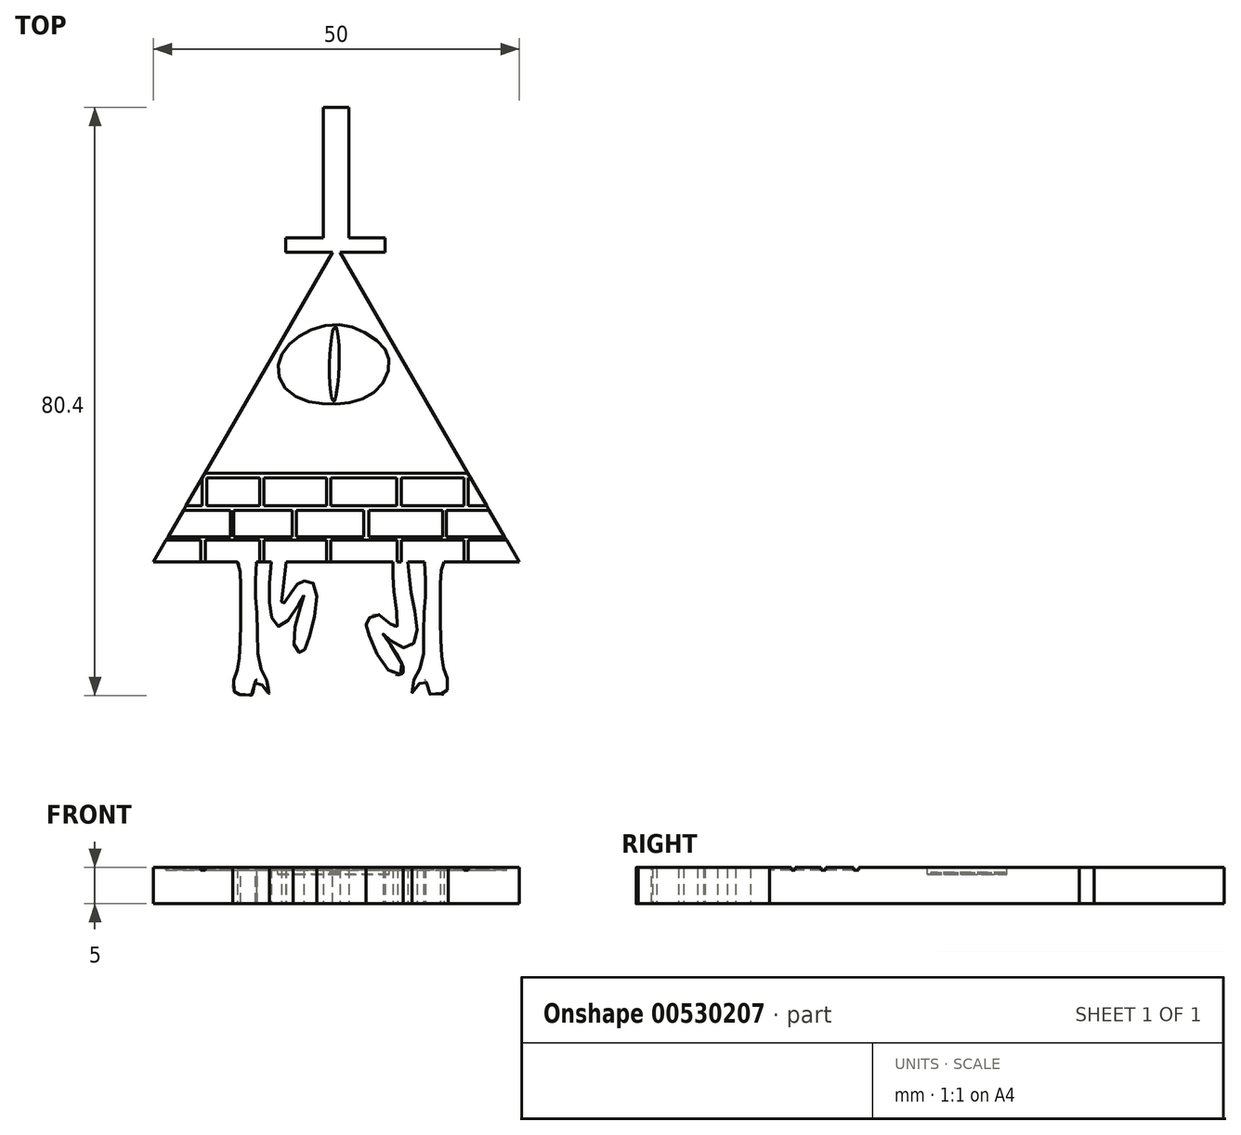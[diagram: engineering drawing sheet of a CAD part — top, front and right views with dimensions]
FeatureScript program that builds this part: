
annotation { "Feature Type Name" : "Feature", "Feature Type Description" : "" }
export const myFeature = defineFeature(function(context is Context, id is Id, definition is map)
    precondition{}
    {
        {
            var Q0;
            Q0=qCreatedBy(makeId("Top.planeOp"),FACE);
            var sketch = newSketch(context, id + "F0", { "sketchPlane" : qUnion([Q0])});
            skLineSegment(sketch, "E0", {"start": v(0, 43.3) * mm, "end": v(-25, 0) * mm});
            skLineSegment(sketch, "E1", {"start": v(-25, 0) * mm, "end": v(25, 0) * mm});
            skLineSegment(sketch, "E2", {"start": v(25, 0) * mm, "end": v(0, 43.3) * mm});
            skLineSegment(sketch, "E3.bottom", {"start": v(-6.91, 44.37) * mm, "end": v(6.68, 44.37) * mm});
            skLineSegment(sketch, "E3.top", {"start": v(-6.91, 42.4) * mm, "end": v(6.68, 42.4) * mm});
            skLineSegment(sketch, "E3.left", {"start": v(-6.91, 44.37) * mm, "end": v(-6.91, 42.4) * mm});
            skLineSegment(sketch, "E3.right", {"start": v(6.68, 44.37) * mm, "end": v(6.68, 42.4) * mm});
            skLineSegment(sketch, "E4.bottom", {"start": v(-1.76, 62.16) * mm, "end": v(1.7, 62.16) * mm});
            skLineSegment(sketch, "E4.top", {"start": v(-1.76, 42.4) * mm, "end": v(1.7, 42.4) * mm});
            skLineSegment(sketch, "E4.left", {"start": v(-1.76, 62.16) * mm, "end": v(-1.76, 42.4) * mm});
            skLineSegment(sketch, "E4.right", {"start": v(1.7, 62.16) * mm, "end": v(1.7, 42.4) * mm});
            skFitSpline(sketch, "E5", {"points": [v(-8.9, 0) * mm, v(-8.8, -7.65) * mm, v(-7.35, -8.7) * mm, v(-4.44, -4.65) * mm, v(-5.9, -10.56) * mm, v(-4.86, -12.43) * mm, v(-3.82, -10.66) * mm, v(-2.99, -3.09) * mm, v(-4.75, -2.67) * mm, v(-5.69, -3.5) * mm, v(-7.35, -5.79) * mm, v(-6.83, 0) * mm], "startDerivative": vector(-6.57, -68.42) * mm, "endDerivative": vector(6.6, 85.35) * mm});
            skFitSpline(sketch, "E6", {"points": [v(7.74, 0) * mm, v(7.95, -4.5) * mm, v(8.14, -8.99) * mm, v(5.66, -7.15) * mm, v(4.23, -8.08) * mm, v(4.23, -9.3) * mm, v(7.54, -15.12) * mm, v(9.17, -14.8) * mm, v(6.4, -9.85) * mm, v(8.68, -11.58) * mm, v(10.84, -10.66) * mm, v(10.34, -4.69) * mm, v(9.8, 0) * mm], "startDerivative": vector(0.32, -42.65) * mm, "endDerivative": vector(-4.02, 37.85) * mm});
            skFitSpline(sketch, "E7.MirrorCS", {"points": [v(12.07, 0.02) * mm, v(12.2, -4.33) * mm, v(11.94, -8.38) * mm, v(11.68, -14) * mm, v(10.63, -16.08) * mm, v(10.46, -17.9) * mm, v(12.03, -15.96) * mm, v(12.73, -18.06) * mm, v(13.26, -17.94) * mm, v(13.7, -18.05) * mm, v(14.2, -17.94) * mm, v(14.6, -18.1) * mm, v(15.3, -17) * mm, v(14.9, -15.24) * mm, v(14.5, -13.53) * mm, v(14.25, -9.74) * mm, v(14.25, -4.51) * mm, v(14.34, -1.18) * mm, v(14.7, -0.1) * mm, v(14.95, 0.02) * mm], "startDerivative": vector(3.73, -56.97) * mm, "endDerivative": vector(17.24, -25.07) * mm});
            skFitSpline(sketch, "E8", {"points": [v(-10.9, 0.02) * mm, v(-11.04, -4.46) * mm, v(-10.78, -8.52) * mm, v(-10.52, -14.14) * mm, v(-9.47, -16.22) * mm, v(-9.3, -18.03) * mm, v(-10.87, -16.1) * mm, v(-11.57, -18.2) * mm, v(-12.1, -18.07) * mm, v(-12.53, -18.18) * mm, v(-13.03, -18.07) * mm, v(-13.45, -18.24) * mm, v(-14.14, -17.14) * mm, v(-13.74, -15.38) * mm, v(-13.34, -13.67) * mm, v(-13.09, -9.88) * mm, v(-13.09, -4.65) * mm, v(-13.17, -1.31) * mm, v(-13.52, 0.02) * mm, v(-13.78, 0.02) * mm], "startDerivative": vector(-3.7, -61.3) * mm, "endDerivative": vector(-17.65, -5.45) * mm});
            skSolve(sketch);
        }
        {
            var Q0;
            Q0=qSketchRegion(id+"F0",true);
            extrude(context, id + "F1", {"entities" : qUnion([Q0]), "depth" : 5 * mm, "offsetDistance" : 25 * mm});
        }
        {
            var Q0;
            Q0=makeQuery(id+"F1.opExtrude","CAP_FACE",FACE,{"disambiguationData":[OSD([sQuery(id+"F0.wireOp",EDGE,"E1"),sQuery(id+"F0.wireOp",EDGE,"E3.bottom"),sQuery(id+"F0.wireOp",EDGE,"E3.top"),sQuery(id+"F0.wireOp",EDGE,"E3.left"),sQuery(id+"F0.wireOp",EDGE,"E3.right"),sQuery(id+"F0.wireOp",EDGE,"E4.bottom"),sQuery(id+"F0.wireOp",EDGE,"E4.top"),sQuery(id+"F0.wireOp",EDGE,"E4.left"),sQuery(id+"F0.wireOp",EDGE,"E4.right"),sQuery(id+"F0.wireOp",EDGE,"E5"),sQuery(id+"F0.wireOp",EDGE,"E6"),sQuery(id+"F0.wireOp",EDGE,"E7.MirrorCS"),sQuery(id+"F0.wireOp",EDGE,"E8"),sQuery(id+"F0.wireOp",EDGE,"E0"),sQuery(id+"F0.wireOp",EDGE,"E2")])],"isStart":false});
            var sketch = newSketch(context, id + "F2", { "sketchPlane" : qUnion([Q0])});
            skFitSpline(sketch, "E9", {"points": [v(-7.95, 26.97) * mm, v(-6.71, 29.45) * mm, v(-4.03, 31.52) * mm, v(-0.1, 32.45) * mm, v(3.43, 31.63) * mm, v(6.45, 29.42) * mm, v(7.24, 27.28) * mm, v(6.14, 24.16) * mm, v(3.23, 22.18) * mm, v(-0.4, 21.62) * mm, v(-4.08, 22.04) * mm, v(-7.17, 24.05) * mm, v(-7.95, 26.97) * mm]});
            skSolve(sketch);
        }
        {
            var Q0;
            Q0=makeQuery(id+"F2.imprint","IMPRINT",FACE,{"disambiguationData":[TD([[makeQuery(id+"F2.imprint","IMPRINT",EDGE,{"derivedFrom":sQuery(id+"F2.wireOp",EDGE,"E9")}),-1.0]])]});
            extrude(context, id + "F3", {"entities" : qUnion([Q0]), "operationType" : NewBodyOperationType.REMOVE, "oppositeDirection" : true, "depth" : 1 * mm, "offsetDistance" : 25 * mm});
        }
        {
            var Q0;
            Q0=makeQuery(id+"F3.boolean.opBoolean","COPY",FACE,{"derivedFrom":makeQuery(id+"F3.opExtrude","CAP_FACE",FACE,{"disambiguationData":[OSD([sQuery(id+"F2.wireOp",EDGE,"E9")])],"isStart":false})});
            var sketch = newSketch(context, id + "F4", { "sketchPlane" : qUnion([Q0])});
            skFitSpline(sketch, "E10", {"points": [v(-0.15, 32.17) * mm, v(-0.02, 32.12) * mm, v(0.4, 28.1) * mm, v(-0.2, 22.18) * mm, v(-0.35, 22.04) * mm, v(-0.54, 22.16) * mm, v(-0.9, 28.03) * mm, v(-0.3, 32.05) * mm, v(-0.15, 32.17) * mm]});
            skSolve(sketch);
        }
        {
            var Q0;
            Q0=qSketchRegion(id+"F4",true);
            extrude(context, id + "F5", {"entities" : qUnion([Q0]), "depth" : 0.3 * mm});
        }
        {
            var Q0;
            Q0=makeQuery(id+"F1.opExtrude","CAP_FACE",FACE,{"disambiguationData":[OSD([sQuery(id+"F0.wireOp",EDGE,"E1"),sQuery(id+"F0.wireOp",EDGE,"E3.bottom"),sQuery(id+"F0.wireOp",EDGE,"E3.top"),sQuery(id+"F0.wireOp",EDGE,"E3.left"),sQuery(id+"F0.wireOp",EDGE,"E3.right"),sQuery(id+"F0.wireOp",EDGE,"E4.bottom"),sQuery(id+"F0.wireOp",EDGE,"E4.top"),sQuery(id+"F0.wireOp",EDGE,"E4.left"),sQuery(id+"F0.wireOp",EDGE,"E4.right"),sQuery(id+"F0.wireOp",EDGE,"E5"),sQuery(id+"F0.wireOp",EDGE,"E6"),sQuery(id+"F0.wireOp",EDGE,"E7.MirrorCS"),sQuery(id+"F0.wireOp",EDGE,"E8"),sQuery(id+"F0.wireOp",EDGE,"E0"),sQuery(id+"F0.wireOp",EDGE,"E2")])],"isStart":false});
            var sketch = newSketch(context, id + "F6", { "sketchPlane" : qUnion([Q0])});
            skLineSegment(sketch, "E11", {"start": v(-23.28, 2.98) * mm, "end": v(23.28, 2.98) * mm});
            skLineSegment(sketch, "E12", {"start": v(23, 3.47) * mm, "end": v(-23, 3.47) * mm});
            skLineSegment(sketch, "E13", {"start": v(-20.92, 7.06) * mm, "end": v(20.92, 7.06) * mm});
            skLineSegment(sketch, "E14", {"start": v(20.55, 7.7) * mm, "end": v(-20.55, 7.7) * mm});
            skLineSegment(sketch, "E15", {"start": v(-18.36, 11.5) * mm, "end": v(18.36, 11.5) * mm});
            skLineSegment(sketch, "E16", {"start": v(17.98, 12.17) * mm, "end": v(-17.97, 12.17) * mm});
            skLineSegment(sketch, "E17", {"start": v(-17.97, 12.17) * mm, "end": v(-18.36, 11.5) * mm});
            skLineSegment(sketch, "E18", {"start": v(18.36, 11.5) * mm, "end": v(17.98, 12.17) * mm});
            skLineSegment(sketch, "E19", {"start": v(20.92, 7.06) * mm, "end": v(20.55, 7.7) * mm});
            skLineSegment(sketch, "E20", {"start": v(23.28, 2.98) * mm, "end": v(23, 3.47) * mm});
            skLineSegment(sketch, "E21", {"start": v(-20.55, 7.7) * mm, "end": v(-20.92, 7.06) * mm});
            skLineSegment(sketch, "E22", {"start": v(-23, 3.47) * mm, "end": v(-23.28, 2.98) * mm});
            skLineSegment(sketch, "E23", {"start": v(-17.92, 2.98) * mm, "end": v(-17.92, 0) * mm});
            skLineSegment(sketch, "E24", {"start": v(-18.54, 2.98) * mm, "end": v(-18.54, 0) * mm});
            skLineSegment(sketch, "E25", {"start": v(-17.92, 0) * mm, "end": v(-18.54, 0) * mm});
            skLineSegment(sketch, "E26", {"start": v(-18.36, 11.5) * mm, "end": v(-18.36, 7.7) * mm});
            skLineSegment(sketch, "E27", {"start": v(-18.36, 11.5) * mm, "end": v(-17.72, 12.6) * mm});
            skLineSegment(sketch, "E28", {"start": v(-14.5, 7.06) * mm, "end": v(-14.5, 3.47) * mm});
            skLineSegment(sketch, "E29", {"start": v(-14.06, 3.47) * mm, "end": v(-14.06, 7.06) * mm});
            skLineSegment(sketch, "E30", {"start": v(-17.72, 11.5) * mm, "end": v(-17.72, 7.7) * mm});
            skLineSegment(sketch, "E31", {"start": v(-10.45, 2.98) * mm, "end": v(-10.45, 0) * mm});
            skLineSegment(sketch, "E32", {"start": v(-9.9, 0) * mm, "end": v(-9.9, 2.98) * mm});
            skLineSegment(sketch, "E33", {"start": v(-9.9, 7.7) * mm, "end": v(-9.9, 11.5) * mm});
            skLineSegment(sketch, "E34", {"start": v(-10.45, 7.7) * mm, "end": v(-10.45, 11.5) * mm});
            skLineSegment(sketch, "E35", {"start": v(-6.05, 7.06) * mm, "end": v(-6.05, 3.47) * mm});
            skLineSegment(sketch, "E36", {"start": v(-5.46, 7.06) * mm, "end": v(-5.46, 3.47) * mm});
            skLineSegment(sketch, "E37", {"start": v(-1.32, 11.5) * mm, "end": v(-1.32, 7.7) * mm});
            skLineSegment(sketch, "E38", {"start": v(-0.76, 11.5) * mm, "end": v(-0.76, 7.7) * mm});
            skLineSegment(sketch, "E39", {"start": v(-0.76, 2.98) * mm, "end": v(-0.76, 0) * mm});
            skLineSegment(sketch, "E40", {"start": v(-1.32, 2.98) * mm, "end": v(-1.32, 0) * mm});
            skLineSegment(sketch, "E41", {"start": v(3.74, 7.06) * mm, "end": v(3.74, 3.47) * mm});
            skLineSegment(sketch, "E42", {"start": v(4.46, 7.06) * mm, "end": v(4.46, 3.47) * mm});
            skLineSegment(sketch, "E43", {"start": v(8.33, 11.5) * mm, "end": v(8.33, 7.7) * mm});
            skLineSegment(sketch, "E44", {"start": v(8.89, 11.5) * mm, "end": v(8.89, 7.7) * mm});
            skLineSegment(sketch, "E45", {"start": v(8.89, 2.98) * mm, "end": v(8.89, 0) * mm});
            skLineSegment(sketch, "E46", {"start": v(8.33, 2.98) * mm, "end": v(8.33, 0) * mm});
            skLineSegment(sketch, "E47", {"start": v(14.55, 7.06) * mm, "end": v(14.55, 3.47) * mm});
            skLineSegment(sketch, "E48", {"start": v(15.03, 7.06) * mm, "end": v(15.03, 3.47) * mm});
            skLineSegment(sketch, "E49", {"start": v(17.46, 11.5) * mm, "end": v(17.46, 7.7) * mm});
            skLineSegment(sketch, "E50", {"start": v(18.02, 11.5) * mm, "end": v(18.02, 7.7) * mm});
            skLineSegment(sketch, "E51", {"start": v(18.02, 2.98) * mm, "end": v(18.02, 0) * mm});
            skLineSegment(sketch, "E52", {"start": v(17.46, 2.98) * mm, "end": v(17.46, 0) * mm});
            skSolve(sketch);
        }
        {
            var Q0;
            Q0=qSketchRegion(id+"F6",true);
            extrude(context, id + "F7", {"entities" : qUnion([Q0]), "operationType" : NewBodyOperationType.REMOVE, "oppositeDirection" : true, "depth" : 0.4 * mm, "offsetDistance" : 25 * mm});
        }
        {
            var Q0;
            {var subQ1=sQuery(id+"F6.wireOp",EDGE,"E30");Q0=makeQuery(id+"F7.boolean.opBoolean","SPLIT",FACE,{"disambiguationData":[TD([makeQuery(id+"F7.opExtrude","SWEPT_FACE",FACE,{"disambiguationData":[OSD([subQ1])]})])],"derivedFrom":makeQuery(id+"F1.opExtrude","CAP_FACE",FACE,{"disambiguationData":[OSD([sQuery(id+"F0.wireOp",EDGE,"E1"),sQuery(id+"F0.wireOp",EDGE,"E3.bottom"),sQuery(id+"F0.wireOp",EDGE,"E3.top"),sQuery(id+"F0.wireOp",EDGE,"E3.left"),sQuery(id+"F0.wireOp",EDGE,"E3.right"),sQuery(id+"F0.wireOp",EDGE,"E4.bottom"),sQuery(id+"F0.wireOp",EDGE,"E4.top"),sQuery(id+"F0.wireOp",EDGE,"E4.left"),sQuery(id+"F0.wireOp",EDGE,"E4.right"),sQuery(id+"F0.wireOp",EDGE,"E5"),sQuery(id+"F0.wireOp",EDGE,"E6"),sQuery(id+"F0.wireOp",EDGE,"E7.MirrorCS"),sQuery(id+"F0.wireOp",EDGE,"E8"),sQuery(id+"F0.wireOp",EDGE,"E0"),sQuery(id+"F0.wireOp",EDGE,"E2")])],"isStart":false})});}
            var sketch = newSketch(context, id + "F8", { "sketchPlane" : qUnion([Q0])});
            skLineSegment(sketch, "E53.bottom", {"start": v(-10.46, 11.5) * mm, "end": v(-9.93, 11.5) * mm});
            skLineSegment(sketch, "E53.top", {"start": v(-10.46, 7.7) * mm, "end": v(-9.93, 7.7) * mm});
            skLineSegment(sketch, "E53.left", {"start": v(-10.46, 11.5) * mm, "end": v(-10.46, 7.7) * mm});
            skLineSegment(sketch, "E53.right", {"start": v(-9.93, 11.5) * mm, "end": v(-9.93, 7.7) * mm});
            skLineSegment(sketch, "E54.bottom", {"start": v(-1.33, 11.5) * mm, "end": v(-0.73, 11.5) * mm});
            skLineSegment(sketch, "E54.top", {"start": v(-1.33, 7.7) * mm, "end": v(-0.73, 7.7) * mm});
            skLineSegment(sketch, "E54.left", {"start": v(-1.33, 11.5) * mm, "end": v(-1.33, 7.7) * mm});
            skLineSegment(sketch, "E54.right", {"start": v(-0.73, 11.5) * mm, "end": v(-0.73, 7.7) * mm});
            skLineSegment(sketch, "E55.bottom", {"start": v(-6.05, 7.06) * mm, "end": v(-5.47, 7.06) * mm});
            skLineSegment(sketch, "E55.top", {"start": v(-6.05, 3.47) * mm, "end": v(-5.47, 3.47) * mm});
            skLineSegment(sketch, "E55.left", {"start": v(-6.05, 7.06) * mm, "end": v(-6.05, 3.47) * mm});
            skLineSegment(sketch, "E55.right", {"start": v(-5.47, 7.06) * mm, "end": v(-5.47, 3.47) * mm});
            skLineSegment(sketch, "E56.bottom", {"start": v(-10.46, 3.03) * mm, "end": v(-9.93, 3.03) * mm});
            skLineSegment(sketch, "E56.top", {"start": v(-10.46, 0) * mm, "end": v(-9.93, 0) * mm});
            skLineSegment(sketch, "E56.left", {"start": v(-10.46, 3.03) * mm, "end": v(-10.46, 0) * mm});
            skLineSegment(sketch, "E56.right", {"start": v(-9.93, 3.03) * mm, "end": v(-9.93, 0) * mm});
            skLineSegment(sketch, "E57.bottom", {"start": v(-1.31, 3.02) * mm, "end": v(-0.74, 3.02) * mm});
            skLineSegment(sketch, "E57.top", {"start": v(-1.31, 0.02) * mm, "end": v(-0.74, 0.02) * mm});
            skLineSegment(sketch, "E57.left", {"start": v(-1.31, 3.02) * mm, "end": v(-1.31, 0.02) * mm});
            skLineSegment(sketch, "E57.right", {"start": v(-0.74, 3.02) * mm, "end": v(-0.74, 0.02) * mm});
            skLineSegment(sketch, "E58.bottom", {"start": v(8.33, 3.03) * mm, "end": v(8.92, 3.03) * mm});
            skLineSegment(sketch, "E58.top", {"start": v(8.33, 0.03) * mm, "end": v(8.92, 0.03) * mm});
            skLineSegment(sketch, "E58.left", {"start": v(8.33, 3.03) * mm, "end": v(8.33, 0.03) * mm});
            skLineSegment(sketch, "E58.right", {"start": v(8.92, 3.03) * mm, "end": v(8.92, 0.03) * mm});
            skLineSegment(sketch, "E59.bottom", {"start": v(17.45, 3.02) * mm, "end": v(18.05, 3.02) * mm});
            skLineSegment(sketch, "E59.top", {"start": v(17.45, -0.02) * mm, "end": v(18.05, -0.02) * mm});
            skLineSegment(sketch, "E59.left", {"start": v(17.45, 3.02) * mm, "end": v(17.45, -0.02) * mm});
            skLineSegment(sketch, "E59.right", {"start": v(18.05, 3.02) * mm, "end": v(18.05, -0.02) * mm});
            skLineSegment(sketch, "E60.bottom", {"start": v(3.75, 7.16) * mm, "end": v(4.46, 7.16) * mm});
            skLineSegment(sketch, "E60.top", {"start": v(3.75, 3.3) * mm, "end": v(4.46, 3.3) * mm});
            skLineSegment(sketch, "E60.left", {"start": v(3.75, 7.16) * mm, "end": v(3.75, 3.3) * mm});
            skLineSegment(sketch, "E60.right", {"start": v(4.46, 7.16) * mm, "end": v(4.46, 3.3) * mm});
            skLineSegment(sketch, "E61.bottom", {"start": v(8.28, 11.8) * mm, "end": v(8.9, 11.8) * mm});
            skLineSegment(sketch, "E61.top", {"start": v(8.28, 7.56) * mm, "end": v(8.9, 7.56) * mm});
            skLineSegment(sketch, "E61.left", {"start": v(8.28, 11.8) * mm, "end": v(8.28, 7.56) * mm});
            skLineSegment(sketch, "E61.right", {"start": v(8.9, 11.8) * mm, "end": v(8.9, 7.56) * mm});
            skSolve(sketch);
        }
        {
            var Q0;
            Q0=qSketchRegion(id+"F8",true);
            extrude(context, id + "F9", {"entities" : qUnion([Q0]), "operationType" : NewBodyOperationType.REMOVE, "oppositeDirection" : true, "depth" : .4 * mm, "offsetDistance" : 25 * mm});
        }
    });
